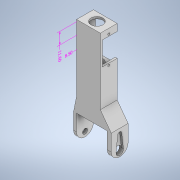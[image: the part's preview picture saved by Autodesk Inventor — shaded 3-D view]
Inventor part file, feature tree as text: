
AUTODESK INVENTOR PART (.ipt)
format: ipt  version: 2022.1 (Build 261234000, 234)  size: 280,576 bytes
history: native  units: mm
features: extrude x15, sketch x15, other x3, fillet x1
ambient origin geometry x8: Origin, YZ Plane, XZ Plane, XY Plane, X Axis, Y Axis, Z Axis, Center Point
bodies: Solid1 (feature_tree)
feature tree (34):
  other  "Annotations"
  extrude  "Extrusion1"  Depth=80.0mm
  extrude  "Extrusion2"  Depth=2.0mm
  extrude  "Extrusion3"  Depth=15.0mm TaperAngle=0.0deg
  extrude  "Extrusion4"  Depth=2.0mm
  extrude  "Extrusion5"  Depth=8.5mm
  extrude  "Extrusion9"  Depth=3.0mm
  extrude  "Extrusion10"  Depth=15.0mm
  extrude  "Extrusion11"  Depth=2.0mm
  extrude  "Extrusion12"  Depth=15.0mm TaperAngle=0.0deg
  extrude  "Extrusion14"  Depth=5.0mm TaperAngle=0.0deg
  extrude  "Extrusion15"  TaperAngle=0.0deg  [1 undecoded]
  extrude  "Extrusion16"  Depth=3.0mm
  extrude  "Extrusion17"  TaperAngle=0.0deg  [1 undecoded]
  extrude  "Extrusion18"  Depth=4.0mm
  fillet  "Fillet2"  Radius=10.0mm
  extrude  "Extrusion19"  TaperAngle=90.0deg  [1 undecoded]
  sketch  "Sketch1"  dims[d0=24.0mm d1=80.0mm]
  sketch  "Sketch2"  dims[d2=2.0mm d3=0.0mm d4=2.0mm]
  sketch  "Sketch3"  dims[d5=2.0mm d6=15.0mm d7=0.0mm]
  sketch  "Sketch4"  dims[d8=2.0mm d9=2.0mm]
  sketch  "Sketch5"  dims[d10=8.5mm d11=8.5mm]
  sketch  "Sketch12"  dims[d12=27.5mm d13=3.0mm]
  sketch  "Sketch13"  dims[d14=12.0mm d15=0.0mm d23=15.0mm]
  sketch  "Sketch14"  dims[d24=23.5mm d25=2.0mm]
  sketch  "Sketch15"  dims[d26=2.0mm d27=15.0mm d28=0.0mm]
  sketch  "Sketch16"  dims[d29=5.0mm d30=5.0mm d31=0.0mm]
  sketch  "Sketch17"  dims[d32=8.6mm d33=0.0mm]
  sketch  "Sketch18"  dims[d51=38.0mm d52=3.0mm]
  sketch  "Sketch19"  dims[d53=25.0mm d54=0.0mm]
  sketch  "Sketch20"  dims[d55=3.0mm d56=4.0mm d57=10.0mm d58=0.0mm]
  sketch  "Sketch21"  dims[d59=15.0mm d60=90.0deg d61=10.0mm d62=0.0mm d63=15.0mm d64=90.0deg d65=5.0mm d66=8.5mm d67=20.0mm d68=20.0mm d69=0.0mm d70=2.0mm d71=10.0mm d72=0.0mm d75=10.0mm d76=0.0mm d77=46.5mm d78=0.0mm d79=2.0mm d80=0.0mm d81=12.0mm d82=12.0mm d83=8.5mm d84=2.0mm d85=0.0mm d86=7.5mm d87=10.0mm d88=0.0mm d89=8.5mm d90=4.0mm d91=15.0mm d92=0.0mm d93=2.0mm d94=0.0mm d36=6.779666mm d37=11.6mm d43=1.279577mm d44=8.5mm]
  other  "Linear Dimension 1"
  other  "Linear Dimension 3"
note: 3 required parameter values undecoded (feature->parameter linkage not recoverable at this tier; creation-order binding heuristic only, values carry confidence <= 0.55)
